# Revit family: Haworth_ActiveComponents_ShelfTileMounted_BUILD
name_source: partatom
category: Furniture Systems
revit_build: Autodesk Revit Architecture 2015 (Build: 20141119_1515(x64)
units: mm (PartAtom-declared; Revit-internal decimal feet)

## types (5) — shared parameters
Actual Depth = 11"
Actual Height = 16"
Actual Mounting Height = 23"
Assembly Code = E2020200
Description = Haworth - Active Components - Shelf Tile Mounted
Manufacturer = Haworth
Max. Width = 72"
Min. Width = 48"
Model = AZST
Revision Number = 1
Size = Verify Final Dim. w/ Haworth
Sustainability Info = https://www.haworth.com
Top Shelves Offset = 24"
URL = http://www.haworth.com
URL - Product = http://www.haworth.com
Warranty = http://www.haworth.com

## per-type parameters (varying)
| type | Actual Width | Top Shelves Width | Width |
| 16h 72w | 72" | 48" | 72" |
| 16h 66w | 66" | 42" | 66" |
| 16h 60w | 60" | 36" | 60" |
| 16h 54w | 54" | 30" | 54" |
| 16h 48w | 48" | 24" | 48" |

## geometry (parser evidence)
native form markers: Sweep x2
no freeform markers — native parametric forms only
